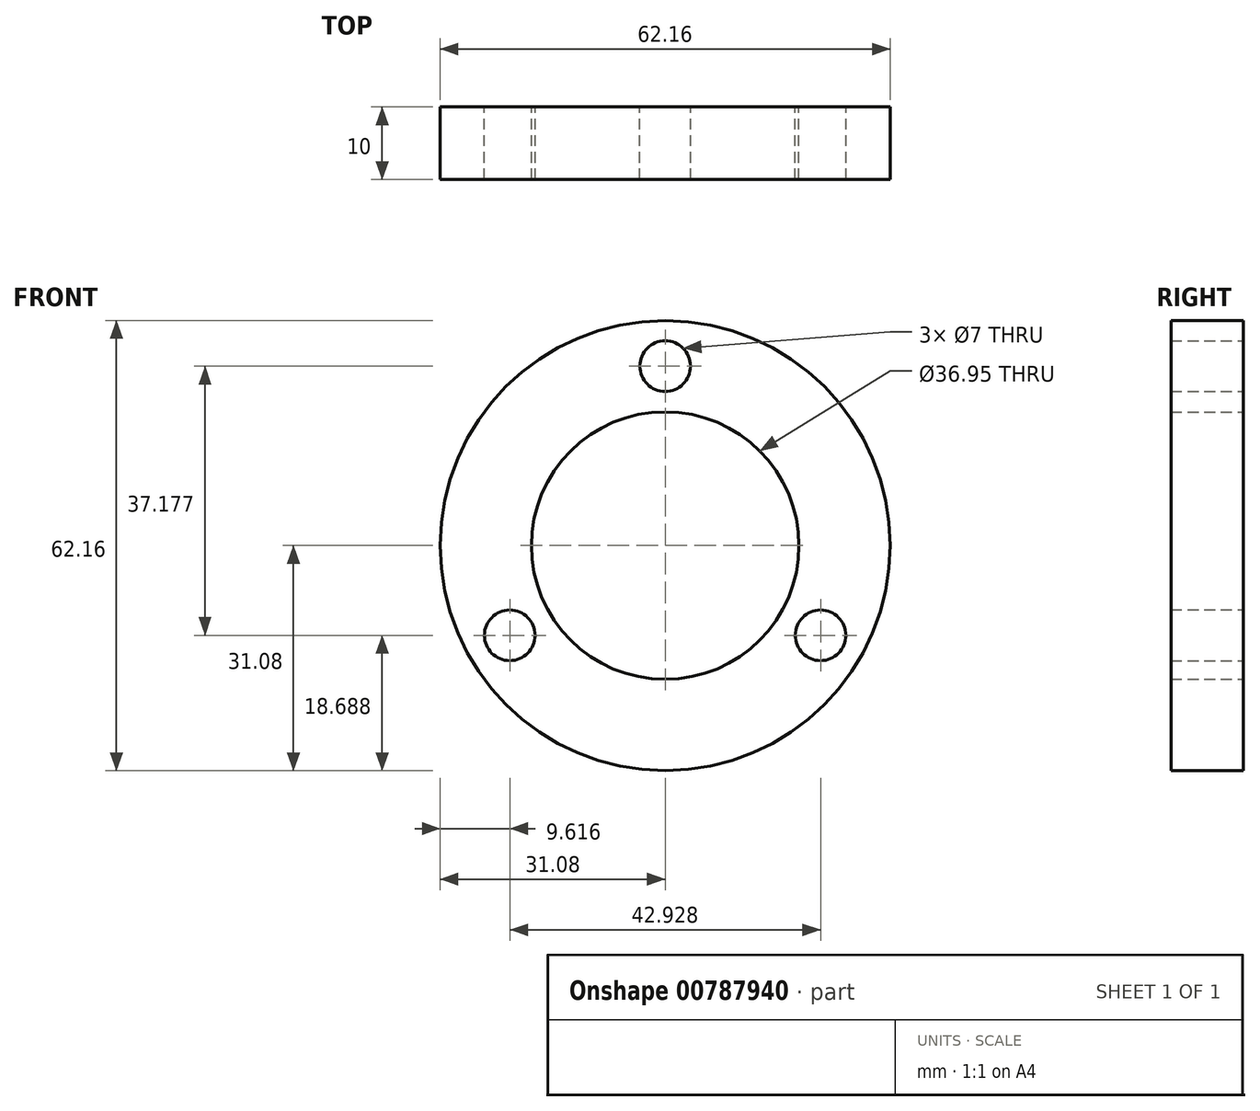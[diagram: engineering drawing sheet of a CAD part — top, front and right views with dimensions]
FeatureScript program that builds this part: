
annotation { "Feature Type Name" : "Feature", "Feature Type Description" : "" }
export const myFeature = defineFeature(function(context is Context, id is Id, definition is map)
    precondition{}
    {
        {
            var Q0;
            Q0=qCreatedBy(makeId("Front.planeOp"),FACE);
            var sketch = newSketch(context, id + "F0", { "sketchPlane" : qUnion([Q0])});
            skCircle(sketch, "E0", {"center": v(0, 0) * mm, "radius": 31.07 * mm});
            skCircle(sketch, "E1", {"center": v(0, 0) * mm, "radius": 18.48 * mm});
            skSolve(sketch);
        }
        {
            var Q0;
            Q0=makeQuery(id+"F0.imprint","IMPRINT",FACE,{"disambiguationData":[TD([[makeQuery(id+"F0.imprint","IMPRINT",EDGE,{"derivedFrom":sQuery(id+"F0.wireOp",EDGE,"E0")}),1.0]])]});
            extrude(context, id + "F1", {"entities" : qUnion([Q0]), "depth" : 10 * mm, "offsetDistance" : 25 * mm});
        }
        {
            var Q0;
            Q0=qCreatedBy(makeId("Front.planeOp"),FACE);
            var sketch = newSketch(context, id + "F2", { "sketchPlane" : qUnion([Q0])});
            skCircle(sketch, "E2", {"center": v(0, 24.78) * mm, "radius": 3.5 * mm});
            skCircle(sketch, "E3", {"center": v(21.46, -12.4) * mm, "radius": 3.5 * mm});
            skCircle(sketch, "E4", {"center": v(-21.46, -12.4) * mm, "radius": 3.5 * mm});
            skSolve(sketch);
        }
        {
            var Q0;
            Q0=makeQuery(id+"F2.imprint","IMPRINT",FACE,{"disambiguationData":[TD([[makeQuery(id+"F2.imprint","IMPRINT",EDGE,{"derivedFrom":sQuery(id+"F2.wireOp",EDGE,"E2")}),1.0]])]});
            var Q1;
            Q1=makeQuery(id+"F2.imprint","IMPRINT",FACE,{"disambiguationData":[TD([[makeQuery(id+"F2.imprint","IMPRINT",EDGE,{"derivedFrom":sQuery(id+"F2.wireOp",EDGE,"E3")}),1.0]])]});
            var Q2;
            Q2=makeQuery(id+"F2.imprint","IMPRINT",FACE,{"disambiguationData":[TD([[makeQuery(id+"F2.imprint","IMPRINT",EDGE,{"derivedFrom":sQuery(id+"F2.wireOp",EDGE,"E4")}),1.0]])]});
            extrude(context, id + "F3", {"entities" : qUnion([Q0, Q1, Q2]), "operationType" : NewBodyOperationType.REMOVE, "depth" : 10 * mm, "offsetDistance" : 25 * mm});
        }
    });
